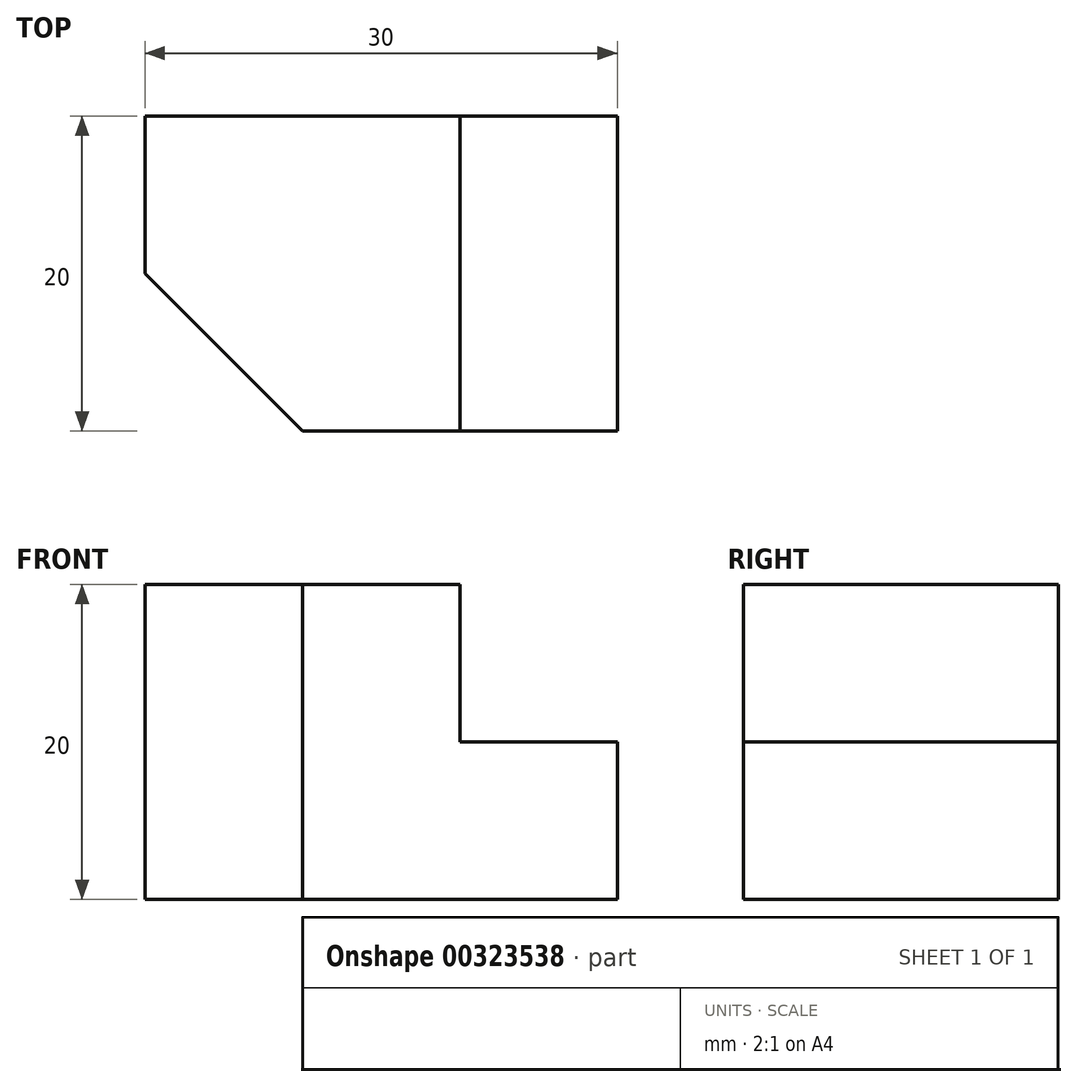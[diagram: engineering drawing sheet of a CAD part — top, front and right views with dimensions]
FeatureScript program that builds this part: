
annotation { "Feature Type Name" : "Feature", "Feature Type Description" : "" }
export const myFeature = defineFeature(function(context is Context, id is Id, definition is map)
    precondition{}
    {
        {
            var Q0;
            Q0=qCreatedBy(makeId("Front.planeOp"),FACE);
            var sketch = newSketch(context, id + "F0", { "sketchPlane" : qUnion([Q0])});
            skLineSegment(sketch, "E0", {"start": v(0, 0) * mm, "end": v(0, 20) * mm});
            skLineSegment(sketch, "E1", {"start": v(0, 20) * mm, "end": v(20, 20) * mm});
            skLineSegment(sketch, "E2", {"start": v(20, 20) * mm, "end": v(20, 10) * mm});
            skLineSegment(sketch, "E3", {"start": v(20, 10) * mm, "end": v(30, 10) * mm});
            skLineSegment(sketch, "E4", {"start": v(30, 10) * mm, "end": v(30, 0) * mm});
            skLineSegment(sketch, "E5", {"start": v(30, 0) * mm, "end": v(0, 0) * mm});
            skLineSegment(sketch, "E6", {"start": v(10, 0) * mm, "end": v(10, 20) * mm});
            skSolve(sketch);
        }
        {
            var Q0;
            {var subQ1=sQuery(id+"F0.wireOp",EDGE,"E2");Q0=makeQuery(id+"F0.imprint","IMPRINT",FACE,{"disambiguationData":[TD([[makeQuery(id+"F0.imprint","IMPRINT",EDGE,{"derivedFrom":subQ1}),-1.0]])]});}
            var Q1;
            {var subQ0=sQuery(id+"F0.wireOp",EDGE,"E0");Q1=makeQuery(id+"F0.imprint","IMPRINT",FACE,{"disambiguationData":[TD([[makeQuery(id+"F0.imprint","IMPRINT",EDGE,{"derivedFrom":subQ0}),-1.0]])]});}
            extrude(context, id + "F1", {"entities" : qUnion([Q0, Q1]), "oppositeDirection" : true, "depth" : 20 * mm});
        }
        {
            var Q0;
            Q0=makeQuery(id+"F1.opExtrude","SWEPT_FACE",FACE,{"disambiguationData":[OSD([sQuery(id+"F0.wireOp",EDGE,"E1")])]});
            var sketch = newSketch(context, id + "F2", { "sketchPlane" : qUnion([Q0])});
            skLineSegment(sketch, "E7", {"start": v(10, 0) * mm, "end": v(0, 10) * mm});
            skLineSegment(sketch, "E8", {"start": v(0, 10) * mm, "end": v(0, 0) * mm});
            skLineSegment(sketch, "E9", {"start": v(0, 0) * mm, "end": v(10, 0) * mm});
            skSolve(sketch);
        }
        {
            var Q0;
            Q0=makeQuery(id+"F2.imprint","IMPRINT",FACE,{"disambiguationData":[TD([[makeQuery(id+"F2.imprint","IMPRINT",EDGE,{"derivedFrom":sQuery(id+"F2.wireOp",EDGE,"E7")}),1.0]])]});
            extrude(context, id + "F3", {"entities" : qUnion([Q0]), "operationType" : NewBodyOperationType.REMOVE, "endBound" : BoundingType.THROUGH_ALL, "oppositeDirection" : true, "depth" : 25 * mm});
        }
    });
